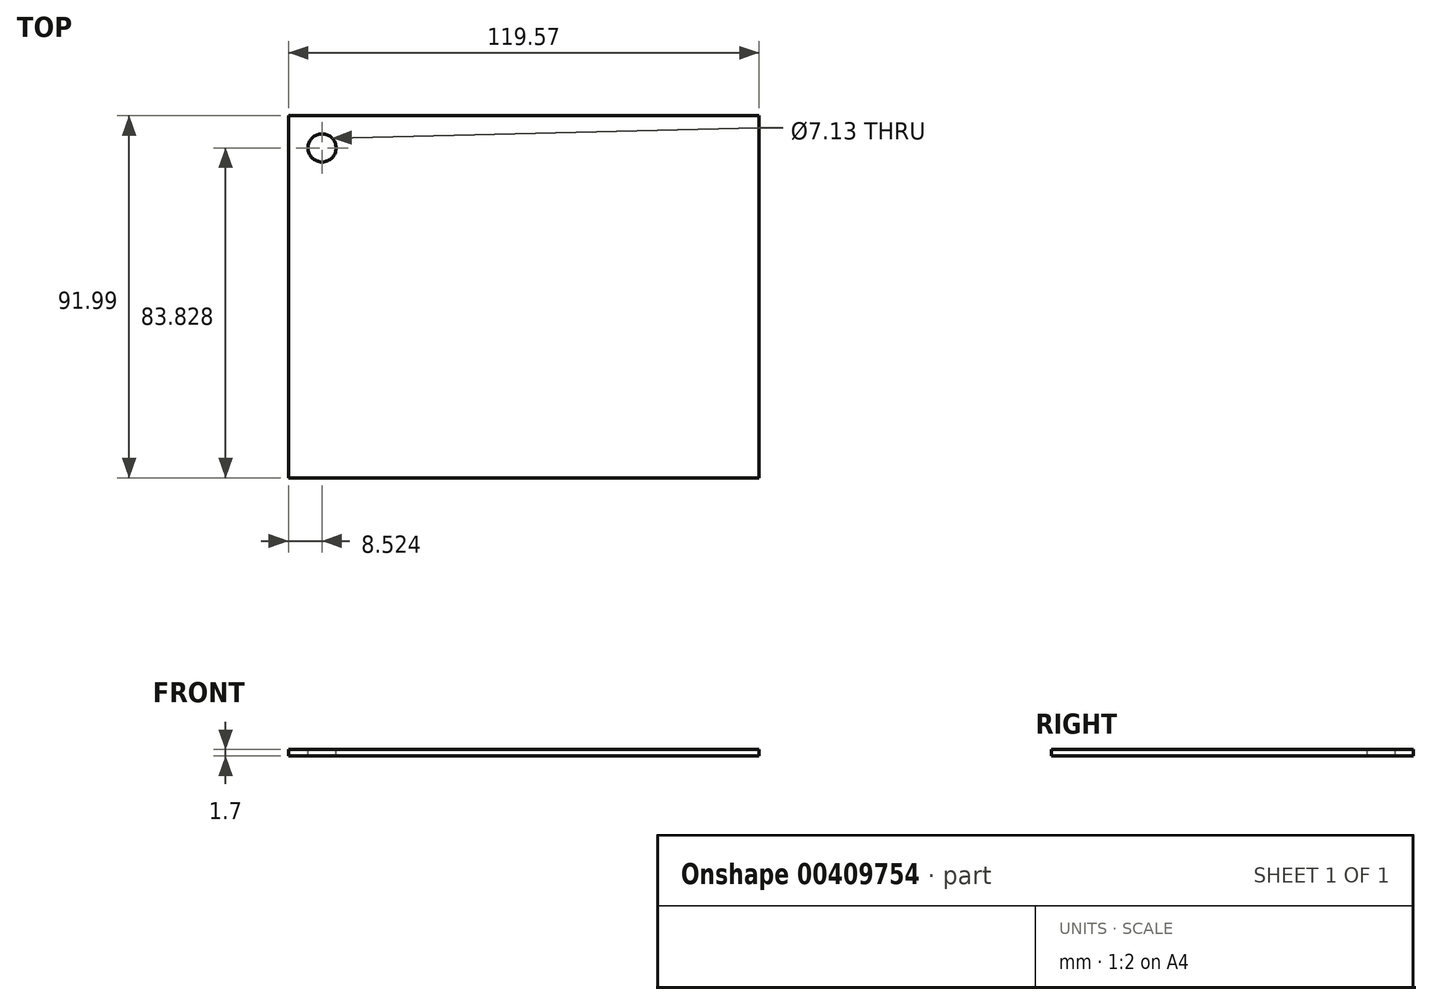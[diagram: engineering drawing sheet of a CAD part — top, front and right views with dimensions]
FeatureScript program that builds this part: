
annotation { "Feature Type Name" : "Feature", "Feature Type Description" : "" }
export const myFeature = defineFeature(function(context is Context, id is Id, definition is map)
    precondition{}
    {
        {
            var Q0;
            Q0=qCreatedBy(makeId("Top.planeOp"),FACE);
            var sketch = newSketch(context, id + "F0", { "sketchPlane" : qUnion([Q0])});
            skLineSegment(sketch, "E0.bottom", {"start": v(-56.8, 45.36) * mm, "end": v(62.78, 45.36) * mm});
            skLineSegment(sketch, "E0.top", {"start": v(-56.8, -46.63) * mm, "end": v(62.78, -46.63) * mm});
            skLineSegment(sketch, "E0.left", {"start": v(-56.8, 45.36) * mm, "end": v(-56.8, -46.63) * mm});
            skLineSegment(sketch, "E0.right", {"start": v(62.78, 45.36) * mm, "end": v(62.78, -46.63) * mm});
            skCircle(sketch, "E1", {"center": v(-48.27, 37.2) * mm, "radius": 3.56 * mm});
            skSolve(sketch);
        }
        {
            var Q0;
            Q0=makeQuery(id+"F0.imprint","IMPRINT",FACE,{"disambiguationData":[TD([[makeQuery(id+"F0.imprint","IMPRINT",EDGE,{"derivedFrom":sQuery(id+"F0.wireOp",EDGE,"E0.bottom")}),-1.0]])]});
            extrude(context, id + "F1", {"entities" : qUnion([Q0]), "oppositeDirection" : true, "depth" : 1.7 * mm});
        }
    });
